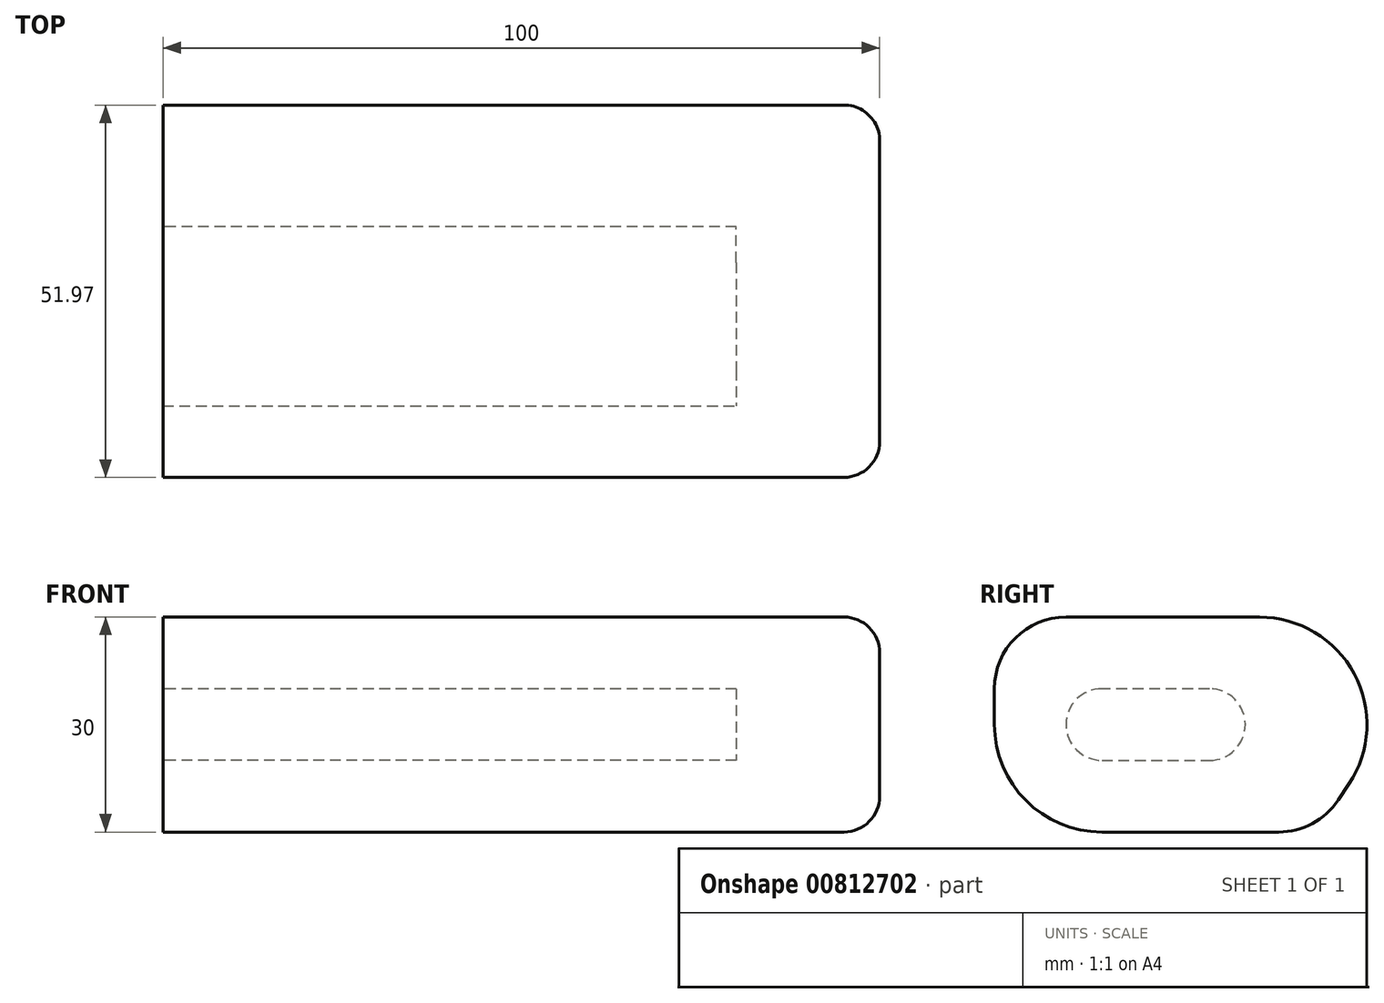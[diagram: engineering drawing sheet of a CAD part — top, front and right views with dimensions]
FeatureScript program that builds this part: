
annotation { "Feature Type Name" : "Feature", "Feature Type Description" : "" }
export const myFeature = defineFeature(function(context is Context, id is Id, definition is map)
    precondition{}
    {
        {
            var Q0;
            Q0=qCreatedBy(makeId("Right.planeOp"),FACE);
            var sketch = newSketch(context, id + "F0", { "sketchPlane" : qUnion([Q0])});
            skLineSegment(sketch, "E0", {"start": v(0, 0) * mm, "end": v(65, 0) * mm});
            skLineSegment(sketch, "E1", {"start": v(0, 0) * mm, "end": v(0, -30) * mm});
            skLineSegment(sketch, "E2", {"start": v(0, -30) * mm, "end": v(45, -30) * mm});
            skLineSegment(sketch, "E3", {"start": v(45, -30) * mm, "end": v(65, 0) * mm});
            skSolve(sketch);
        }
        {
            var Q0;
            Q0=makeQuery(id+"F0.imprint","IMPRINT",FACE,{"disambiguationData":[TD([[makeQuery(id+"F0.imprint","IMPRINT",EDGE,{"derivedFrom":sQuery(id+"F0.wireOp",EDGE,"E0")}),-1.0]])]});
            extrude(context, id + "F1", {"entities" : qUnion([Q0]), "depth" : 100 * mm, "offsetDistance" : 25 * mm});
        }
        {
            var Q0;
            Q0=makeQuery(id+"F1.opExtrude","CAP_FACE",FACE,{"disambiguationData":[OSD([sQuery(id+"F0.wireOp",EDGE,"E0"),sQuery(id+"F0.wireOp",EDGE,"E1"),sQuery(id+"F0.wireOp",EDGE,"E2"),sQuery(id+"F0.wireOp",EDGE,"E3")])],"isStart":true});
            var sketch = newSketch(context, id + "F2", { "sketchPlane" : qUnion([Q0])});
            skLineSegment(sketch, "E4", {"start": v(0, 27.9) * mm, "end": v(0, -73.39) * mm});
            skLineSegment(sketch, "E5", {"start": v(-45, 27.9) * mm, "end": v(-45, -97.43) * mm});
            skLineSegment(sketch, "E6", {"start": v(-35, 27.54) * mm, "end": v(-35, -58.72) * mm});
            skLineSegment(sketch, "E7", {"start": v(-10, 30.54) * mm, "end": v(-10, -52.73) * mm});
            skLineSegment(sketch, "E8", {"start": v(-59.87, 0) * mm, "end": v(23.4, 0) * mm});
            skLineSegment(sketch, "E9", {"start": v(21.6, -20) * mm, "end": v(-83.54, -20) * mm});
            skLineSegment(sketch, "E10", {"start": v(-79.04, -10) * mm, "end": v(54.25, -10) * mm});
            skSolve(sketch);
        }
        {
            var Q0;
            {var subQ0=sQuery(id+"F2.wireOp",EDGE,"E10");var subQ1=sQuery(id+"F2.wireOp",EDGE,"E6");var subQ2=makeQuery(id+"F2.imprint","INTERSECT",VERTEX,{"derivedFrom":[subQ1,subQ0]});Q0=makeQuery(id+"F2.imprint","IMPRINT",FACE,{"disambiguationData":[TD([[makeQuery(id+"F2.imprint","IMPRINT",EDGE,{"disambiguationData":[TD([[subQ2,-1.0]])],"derivedFrom":subQ1}),1.0]])]});}
            extrude(context, id + "F3", {"entities" : qUnion([Q0]), "operationType" : NewBodyOperationType.REMOVE, "oppositeDirection" : true, "depth" : 80 * mm, "offsetDistance" : 25 * mm});
        }
        {
            var Q0;
            Q0=makeQuery(id+"F3.boolean.opBoolean","COPY",EDGE,{"derivedFrom":makeQuery(id+"F3.opExtrude","SWEPT_EDGE",EDGE,{"disambiguationData":[OSD([sQuery(id+"F2.wireOp",EDGE,"E7"),sQuery(id+"F2.wireOp",EDGE,"E10")])]})});
            var Q1;
            Q1=makeQuery(id+"F3.boolean.opBoolean","COPY",EDGE,{"derivedFrom":makeQuery(id+"F3.opExtrude","SWEPT_EDGE",EDGE,{"disambiguationData":[OSD([sQuery(id+"F2.wireOp",EDGE,"E6"),sQuery(id+"F2.wireOp",EDGE,"E10")])]})});
            var Q2;
            Q2=makeQuery(id+"F3.boolean.opBoolean","COPY",EDGE,{"derivedFrom":makeQuery(id+"F3.opExtrude","SWEPT_EDGE",EDGE,{"disambiguationData":[OSD([sQuery(id+"F2.wireOp",EDGE,"E6"),sQuery(id+"F2.wireOp",EDGE,"E9")])]})});
            var Q3;
            Q3=makeQuery(id+"F3.boolean.opBoolean","COPY",EDGE,{"derivedFrom":makeQuery(id+"F3.opExtrude","SWEPT_EDGE",EDGE,{"disambiguationData":[OSD([sQuery(id+"F2.wireOp",EDGE,"E7"),sQuery(id+"F2.wireOp",EDGE,"E9")])]})});
            fillet(context, id + "F4", {"entities" : qUnion([Q0, Q1, Q2, Q3]), "radius" : 5 * mm, "tangentPropagation" : true, "allowEdgeOverflow" : false});
        }
        {
            var Q0;
            Q0=makeQuery(id+"F1.opExtrude","SWEPT_EDGE",EDGE,{"disambiguationData":[OSD([sQuery(id+"F0.wireOp",EDGE,"E0"),sQuery(id+"F0.wireOp",EDGE,"E3")])]});
            var Q1;
            Q1=makeQuery(id+"F1.opExtrude","SWEPT_EDGE",EDGE,{"disambiguationData":[OSD([sQuery(id+"F0.wireOp",EDGE,"E1"),sQuery(id+"F0.wireOp",EDGE,"E2")])]});
            fillet(context, id + "F5", {"entities" : qUnion([Q0, Q1]), "radius" : 15 * mm, "tangentPropagation" : true, "allowEdgeOverflow" : false});
        }
        {
            var Q0;
            Q0=makeQuery(id+"F1.opExtrude","SWEPT_EDGE",EDGE,{"disambiguationData":[OSD([sQuery(id+"F0.wireOp",EDGE,"E0"),sQuery(id+"F0.wireOp",EDGE,"E1")])]});
            var Q1;
            Q1=makeQuery(id+"F1.opExtrude","SWEPT_EDGE",EDGE,{"disambiguationData":[OSD([sQuery(id+"F0.wireOp",EDGE,"E2"),sQuery(id+"F0.wireOp",EDGE,"E3")])]});
            fillet(context, id + "F6", {"entities" : qUnion([Q0, Q1]), "radius" : 10 * mm, "tangentPropagation" : true, "allowEdgeOverflow" : false});
        }
        {
            var Q0;
            Q0=makeQuery(id+"F1.opExtrude","CAP_EDGE",EDGE,{"disambiguationData":[OSD([sQuery(id+"F0.wireOp",EDGE,"E0")])],"isStart":false});
            fillet(context, id + "F7", {"entities" : qUnion([Q0]), "radius" : 5 * mm, "tangentPropagation" : true, "allowEdgeOverflow" : false});
        }
    });
